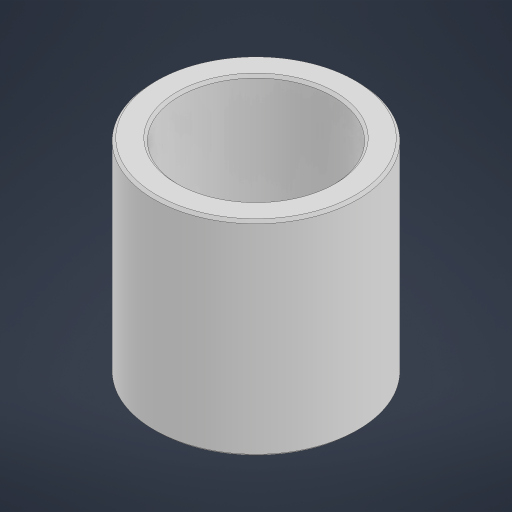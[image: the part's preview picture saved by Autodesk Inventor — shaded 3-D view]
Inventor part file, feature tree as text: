
AUTODESK INVENTOR PART (.ipt)
format: ipt  version: 2023 (Build 270158000, 158)  size: 173,056 bytes
history: native  units: in
note: dims shown in document units (in); Inventor stores cm internally (conversion verified against a paired STEP export)
features: chamfer x1
ambient origin geometry x8: Origin, YZ Plane, XZ Plane, XY Plane, X Axis, Y Axis, Z Axis, Center Point
bodies: Solid1 (feature_tree)
feature tree (1):
  chamfer  "Chamfer1"  [1 undecoded]
note: 1 required parameter value undecoded (feature->parameter linkage not recoverable at this tier; creation-order binding heuristic only, values carry confidence <= 0.55)
